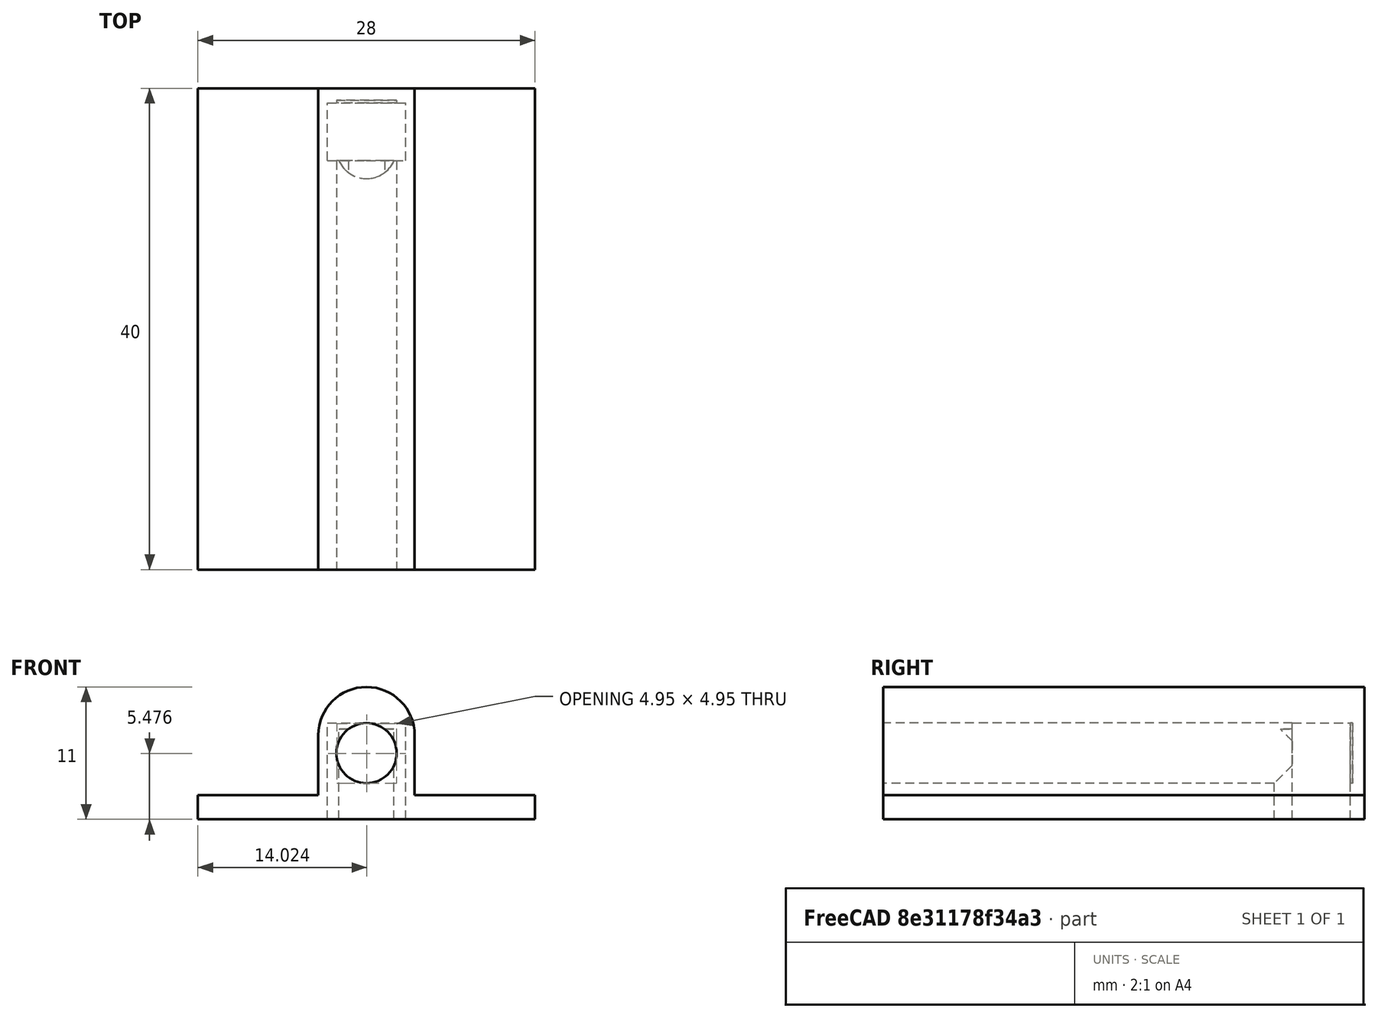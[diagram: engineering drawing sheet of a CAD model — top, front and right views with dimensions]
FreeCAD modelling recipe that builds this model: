
FCSTD DOCUMENT  (FreeCAD 0.15R4671 (Git))
Label: Sense_Beam_Rx
License: All rights reserved
LicenseURL: http://en.wikipedia.org/wiki/All_rights_reserved
objects: Part::Cylinder×4, Part::Box×4, Part::Cut×3, Part::MultiFuse×3, Drawing::FeatureViewPart×2, Drawing::FeatureViewPython×2, Drawing::FeaturePage×1
note: 14 computed .brp shape members not serialized (recipe doc carries the construction recipe); baked Part::Feature solids carry a one-line shape summary decoded from their .brp

FEATURE [Part::Cylinder] Cylinder
  Angle = 360
  Height = 40
  Placement = pos=(28,45,11) rot=(1,0,0;1.5708rad)
  Radius = 4
FEATURE [Part::Cylinder] Cylinder001
  Angle = 360
  Height = 39
  Placement = pos=(28,44,9.5) rot=(1,0,0;1.5708rad)
  Radius = 2.5
FEATURE [Part::Box] Box002  label="PCB"
  Height = 2
  Length = 10
  Placement = pos=(32,5,4) rot=(0,0,1;0rad)
  Width = 40
FEATURE [Part::Box] Box  label="base"
  Height = 7
  Length = 8
  Placement = pos=(24,5,4) rot=(0,0,1;0rad)
  Width = 40
FEATURE [Part::Cylinder] Cylinder002  label="Base_cut"
  Angle = 360
  Height = 40
  Placement = pos=(28,45,11) rot=(1,0,0;1.5708rad)
  Radius = 4
FEATURE [Part::Cut] Cut
  Base = -> Box
  Tool = -> Cylinder002
FEATURE [Part::Cut] Cut001
  Base = -> Cylinder
  Tool = -> Cylinder001
FEATURE [Part::MultiFuse] Fusion
  Shapes = -> [Cut001,Cut]
FEATURE [Part::Box] Box003  label="Cube"
  Height = 8
  Length = 6.5
  Placement = pos=(-0.25,0,0) rot=(0,0,1;0rad)
  Width = 4.8
FEATURE [Part::Cylinder] Cylinder003  label="Cylinder002"
  Angle = 360
  Height = 7.5
  Placement = pos=(3,1,0) rot=(0,0,1;0rad)
  Radius = 2.5
FEATURE [Part::MultiFuse] Fusion001  label="Rx Module"
  Placement = pos=(25,39,4) rot=(0,0,1;0rad)
  Shapes = -> [Cylinder003,Box003]
FEATURE [Part::Cut] Cut002
  Base = -> Fusion
  Tool = -> Fusion001
FEATURE [Part::Box] Box004  label="PCB001"
  Height = 2
  Length = 10
  Placement = pos=(14,5,4) rot=(0,0,1;0rad)
  Width = 40
FEATURE [Part::MultiFuse] Fusion002
  Shapes = -> [Box002,Cut002,Box004]
FEATURE [Drawing::FeatureViewPart] Ortho  label="Ortho_0_0"
  Direction = (1,0,0)
  HiddenWidth = 0.15
  LineWidth = 0.35
  Rotation = -90
  Scale = 3
  ShowHiddenLines = false
  ShowSmoothLines = false
  Source = -> Fusion002
  Tolerance = 0.05
  ViewResult = <g id="Ortho_0_0"\n   transform="rotate(-90,127.667,108.5) translate(127.667,108.5) scale(3,3)"\n  >\n<g   stroke="rgb(0, 0, 0)"\n   stroke-width="0.116667"\n   stroke-linecap="butt"\n   stroke-linejoin="miter"\n   fill="none"\n   transform="scale(1,-1)"\n  >\n<path id= "1" d=" M 15 -45 L 15 -5 " />\n</g>\n<g   stroke="rgb(0, 0, 0)"\n   stroke-width="0.116667"\n   stroke-linecap="butt"\n   stroke-linejoin="miter"\n   fill="none"\n   transform="scale(1,-1)"\n  >\n<path id= "1" d=" M 6 -5 L 11 -5 " />\n<path id= "2" d=" M 6 -45 L 11 -45 " />\n<path id= "3" d=" M 4 -5 L 6 -5 " />\n<path id= "4" d=" M 11 -45 L 11 -5 " />\n<path id= "5" d=" M 6 -5 L 6 -45 " />\n<path d="M11,-5 L11.4479,-5  L11.8901,-5  L12.3211,-5  L12.7355,-5  L13.1281,-5  L13.494,-5  L13.8284,-5  L14.1273,-5  L14.3869,-5  L14.6039,-5  L14.7755,-5  L14.8997,-5  L14.9748,-5  L15,-5 " /><path d="M11,-45 L11.4479,-45  L11.8901,-45  L12.3211,-45  L12.7355,-45  L13.1281,-45  L13.494,-45  L13.8284,-45  L14.1273,-45  L14.3869,-45  L14.6039,-45  L14.7755,-45  L14.8997,-45  L14.9748,-45  L15,-45 " /><path id= "8" d=" M 4 -45 L 6 -45 " />\n<path id= "9" d=" M 4 -5 L 4 -45 " />\n<path id= "10" d=" M 6 -5 L 6 -45 " />\n</g>\n</g>
  Visible = true
  X = 127.667
  Y = 108.5
FEATURE [Drawing::FeatureViewPart] Ortho004  label="Ortho_-1_0"
  Direction = (0,-1,0)
  HiddenWidth = 0.15
  LineWidth = 0.35
  Rotation = 90
  Scale = 3
  ShowHiddenLines = false
  ShowSmoothLines = false
  Source = -> Fusion002
  Tolerance = 0.05
  ViewResult = <g id="Ortho_-1_0"\n   transform="rotate(90,-7.66666,108.5) translate(-7.66666,108.5) scale(3,3)"\n  >\n<g   stroke="rgb(0, 0, 0)"\n   stroke-width="0.116667"\n   stroke-linecap="butt"\n   stroke-linejoin="miter"\n   fill="none"\n   transform="scale(1,-1)"\n  >\n<path id= "1" d=" M -4 14 L -6 14 " />\n<path id= "2" d=" M -4 14 L -4 24 " />\n<path id= "3" d=" M -4 24 L -6 24 " />\n<path id= "4" d=" M -6 14 L -6 24 " />\n<path id= "5" d=" M -4 32 L -6 32 " />\n<path id= "6" d=" M -4 24 L -4 32 " />\n<path id= "7" d=" M -6 32 L -11 32 " />\n<path d="M-7 28 A4 4 0 0 1 -11 32" /><path id= "9" d=" M -6 24 L -11 24 " />\n<path d="M-11 24 A4 4 0 0 1 -7 28" /><path id= "11" d=" M -4 32 L -4 42 " />\n<path id= "12" d=" M -4 42 L -6 42 " />\n<path id= "13" d=" M -6 32 L -6 42 " />\n<path d="M-11 32 A4 4 0 0 1 -11 24" /><path d="M-7 28 A2.5 2.5 0 0 1 -9.5 30.5" /><path d="M-9.5 30.5 A2.5 2.5 0 1 1 -7 28" /><path d="M-9.5 30.5 A2.5 2.5 0 0 1 -12 28" /><path d="M-12 28 A2.5 2.5 0 0 1 -7 27.9988" /></g>\n</g>
  Visible = true
  X = -7.66666
  Y = 108.5
FEATURE [Drawing::FeatureViewPython] centerLines  # drawing view (typed FeaturePython)
  Rotation = 0
  ViewResult = <g transform="scale(3.000000,3.000000)" stroke="rgb(0,0,255)"  stroke-width="0.106667" > <path d="M 25.444447,26.166667 L 25.444447,25.166667 M 25.444447,24.500000 L 25.444447,23.203841 "/>\n<path d="M 25.444447,26.166667 L 26.444447,26.166667 M 27.111113,26.166667 L 29.111113,26.166667 M 29.777780,26.166667 L 30.558063,26.166667 "/>\n<path d="M 25.444447,26.166667 L 25.444447,27.166667 M 25.444447,27.833333 L 25.444447,29.036500 "/>\n<path d="M 25.444447,26.166667 L 24.444447,26.166667 M 23.777780,26.166667 L 21.777780,26.166667 M 21.111113,26.166667 L 20.111113,26.166667 "/> </g> 
  Visible = true
  X = 0
  Y = 0
  centerLine_color = rgb(0,0,255)
  centerLine_len_dash = 6
  centerLine_len_dot = 3
  centerLine_len_gap = 2
  centerLine_width = 0.32
  click1_x = 91.6742
  click1_y = 69.6115
  click2_x = 59.5312
  click2_y = 87.1095
FEATURE [Drawing::FeatureViewPython] dim  # drawing view (typed FeaturePython)
  Rotation = 0
  ViewResult = <g> \n  <line x1="93.674189" y1="78.500001" x2="97.238880" y2="78.500001" style="stroke:rgb(0,0,255);stroke-width:0.50" />\n<line x1="90.333340" y1="96.500000" x2="97.238880" y2="96.500000" style="stroke:rgb(0,0,255);stroke-width:0.50" />\n<line x1="96.238880" y1="78.500001" x2="96.238880" y2="96.500000" style="stroke:rgb(0,0,255);stroke-width:0.50" /> \n  <polygon points="96.238880,96.500000 97.238880,93.500000 96.238880,92.500000 95.238880,93.500000" style="fill:rgb(0,0,255);stroke:rgb(0,0,255);stroke-width:0" /><polygon points="96.238880,78.500001 95.238880,81.500001 96.238880,82.500001 97.238880,81.500001" style="fill:rgb(0,0,255);stroke:rgb(0,0,255);stroke-width:0" /> \n  <text x="94.238880" y="87.500000" font-family="inherit" font-size="3.6" fill="rgb(0,0,255)" text-anchor="middle" transform="rotate(-90.000000 94.238880,87.500000)" >6</text> </g>
  Visible = true
  X = 0
  Y = 0
  arrowL1 = 3
  arrowL2 = 1
  arrowW = 2
  arrow_scheme = 0
  autoPlaceOffset = 2
  autoPlaceText = true
  click1_x = 96.2389
  click1_y = 87.6801
  click2_x = 96.2389
  click2_y = 87.6801
  comma_decimal_place = false
  dimension_line_overshoot = 1
  gap_datum_points = 2
  halfDimension_linear = false
  lineColor = rgb(0,0,255)
  strokeWidth = 0.5
  textFormat_linear = %(value)3.3f
  textRenderer_color = rgb(0,0,255)
  textRenderer_family = inherit
  textRenderer_size = 3.6
  unit_custom_scale = 1
  unit_scheme = 0
FEATURE [Drawing::FeaturePage] Page
  EditableTexts = Designed by Name | Date | Scale | Weight | Title | Subtitle | Drawing number | Sheet
  Group = -> [Ortho,Ortho004,centerLines,dim]
  Template = <path>
note: 1 file-system path scrubbed to <path> (originals preserved in the JSON sidecar)
